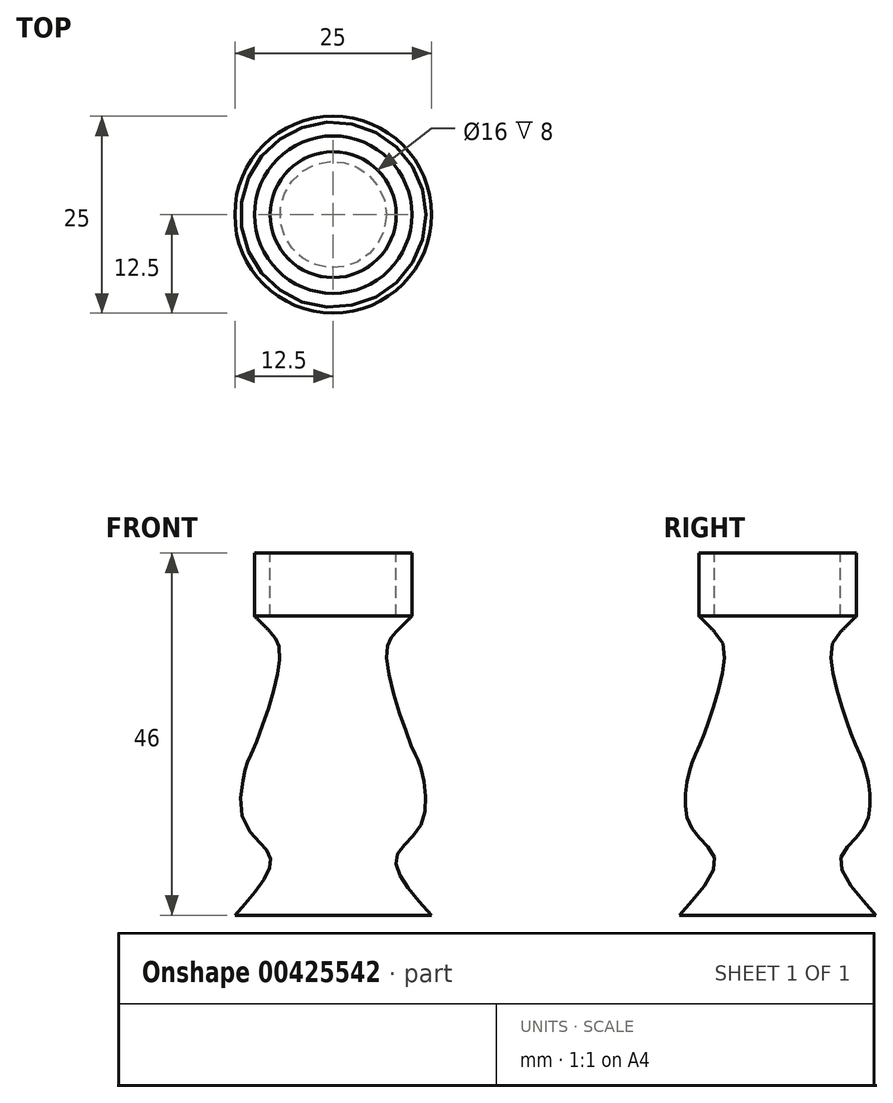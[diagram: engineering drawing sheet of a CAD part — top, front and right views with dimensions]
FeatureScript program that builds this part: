
annotation { "Feature Type Name" : "Feature", "Feature Type Description" : "" }
export const myFeature = defineFeature(function(context is Context, id is Id, definition is map)
    precondition{}
    {
        {
            var Q0;
            Q0=qCreatedBy(makeId("Front.planeOp"),FACE);
            var sketch = newSketch(context, id + "F0", { "sketchPlane" : qUnion([Q0])});
            skLineSegment(sketch, "E0.bottom", {"start": v(0, 0) * mm, "end": v(12.5, 0) * mm});
            skLineSegment(sketch, "E0.top", {"start": v(0, 48) * mm, "end": v(12.5, 48) * mm});
            skLineSegment(sketch, "E0.left", {"start": v(0, 0) * mm, "end": v(0, 48) * mm});
            skLineSegment(sketch, "E0.right", {"start": v(12.5, 0) * mm, "end": v(12.5, 48) * mm});
            skLineSegment(sketch, "E1.bottom", {"start": v(0, 48) * mm, "end": v(8, 48) * mm});
            skLineSegment(sketch, "E1.top", {"start": v(0, 40) * mm, "end": v(8, 40) * mm});
            skLineSegment(sketch, "E1.left", {"start": v(0, 48) * mm, "end": v(0, 40) * mm});
            skLineSegment(sketch, "E1.right", {"start": v(8, 48) * mm, "end": v(8, 40) * mm});
            skLineSegment(sketch, "E2", {"start": v(10, 48) * mm, "end": v(10, 38) * mm});
            skLineSegment(sketch, "E3", {"start": v(10, 38) * mm, "end": v(0, 38) * mm});
            skPoint(sketch, "E4.endSnap0", {"position": v(6.25, 48) * mm});
            skLineSegment(sketch, "E5", {"start": v(10, 40) * mm, "end": v(8, 38) * mm});
            skLineSegment(sketch, "E6", {"start": v(0, 42.26) * mm, "end": v(8, 42.26) * mm});
            skLineSegment(sketch, "E7", {"start": v(0, 2) * mm, "end": v(12.5, 2) * mm});
            skFitSpline(sketch, "E8", {"points": [v(10, 40) * mm, v(8, 38) * mm, v(6.75, 35.2) * mm, v(10, 23.4) * mm, v(10.96, 21.18) * mm, v(11.31, 13.81) * mm, v(8, 9.26) * mm, v(12.5, 2) * mm], "startDerivative": vector(-20.23, -19.95) * mm, "endDerivative": vector(41.32, -45.36) * mm});
            skSolve(sketch);
        }
        {
            var Q0;
            {var subQ3=sQuery(id+"F0.wireOp",EDGE,"E7");Q0=makeQuery(id+"F0.imprint","IMPRINT",FACE,{"disambiguationData":[TD([[makeQuery(id+"F0.imprint","IMPRINT",EDGE,{"derivedFrom":subQ3}),1.0]])]});}
            var Q1;
            {var subQ6=sQuery(id+"F0.wireOp",EDGE,"E1.top");Q1=makeQuery(id+"F0.imprint","IMPRINT",FACE,{"disambiguationData":[TD([[makeQuery(id+"F0.imprint","IMPRINT",EDGE,{"derivedFrom":subQ6}),-1.0]])]});}
            var Q2;
            Q2=sQuery(id+"F0.wireOp",EDGE,"E1.left");
            revolve(context, id + "F1", {"entities" : qUnion([Q0, Q1]), "axis" : qUnion([Q2]), "revolveType" : RevolveType.FULL});
        }
    });
